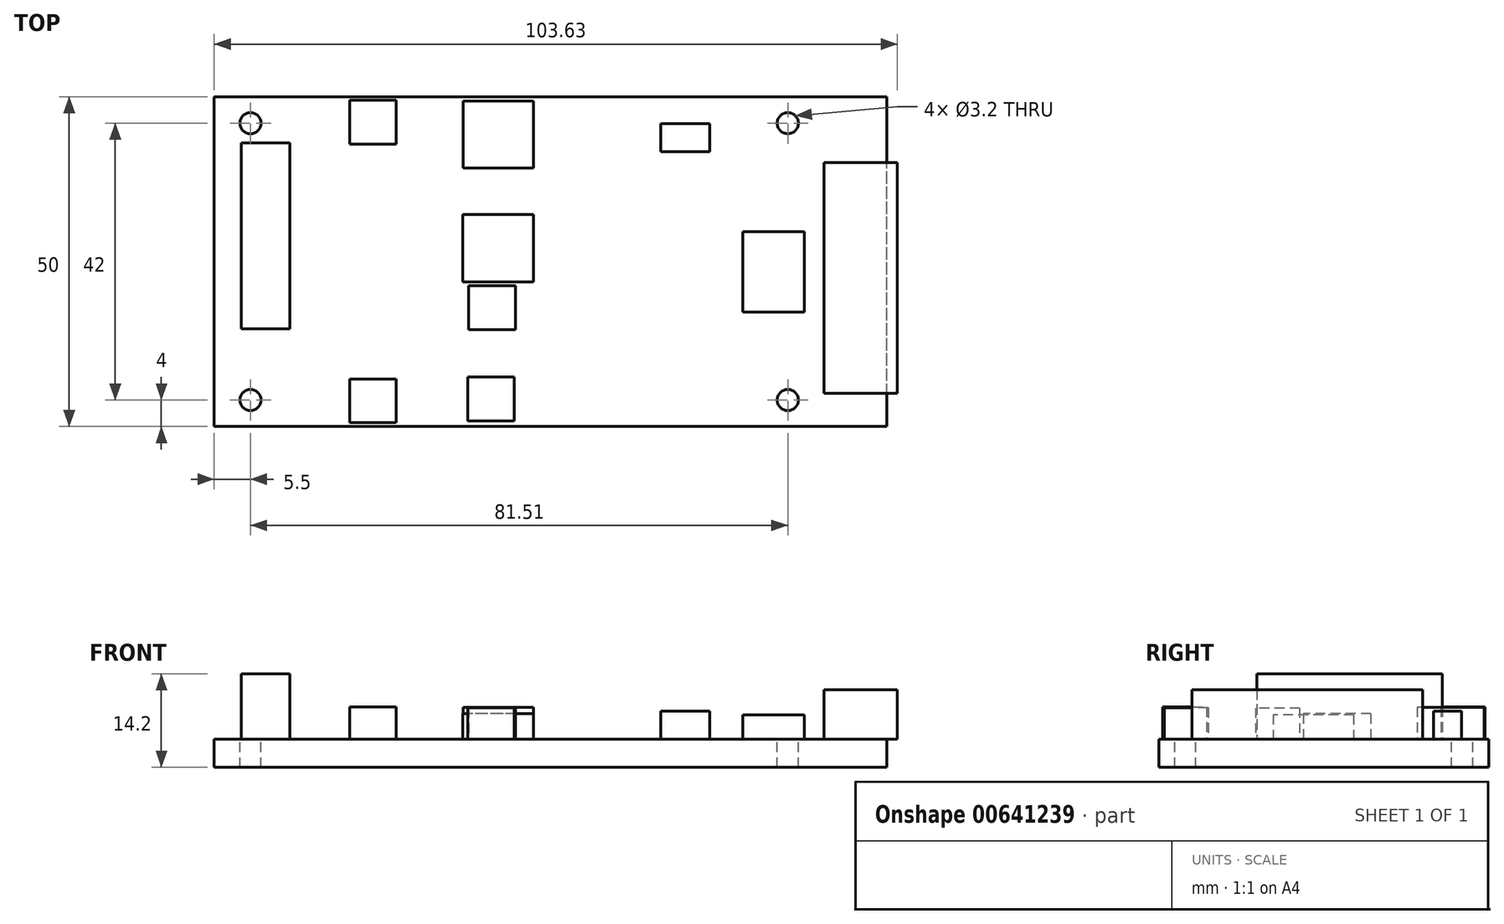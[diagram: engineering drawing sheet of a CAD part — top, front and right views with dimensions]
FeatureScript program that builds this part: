
annotation { "Feature Type Name" : "Feature", "Feature Type Description" : "" }
export const myFeature = defineFeature(function(context is Context, id is Id, definition is map)
    precondition{}
    {
        {
            var Q0;
            Q0=qCreatedBy(makeId("Top.planeOp"),FACE);
            var sketch = newSketch(context, id + "F0", { "sketchPlane" : qUnion([Q0])});
            skLineSegment(sketch, "E0.bottom", {"start": v(51, -25) * mm, "end": v(-51, -25) * mm});
            skLineSegment(sketch, "E0.top", {"start": v(51, 25) * mm, "end": v(-51, 25) * mm});
            skLineSegment(sketch, "E0.left", {"start": v(51, -25) * mm, "end": v(51, 25) * mm});
            skLineSegment(sketch, "E0.right", {"start": v(-51, -25) * mm, "end": v(-51, 25) * mm});
            skPoint(sketch, "E0.middle", {"position": v(0, 0) * mm});
            skSolve(sketch);
        }
        {
            var Q0;
            Q0 = qSketchRegion(id + "F0", true);
            extrude(context, id + "F1", {"entities" : qUnion([Q0]), "depth" : 4.27 * mm, "offsetDistance" : 25 * mm});
        }
        {
            var Q0;
            Q0=makeQuery(id+"F1.opExtrude","CAP_FACE",FACE,{"disambiguationData":[OSD([sQuery(id+"F0.wireOp",EDGE,"E0.bottom"),sQuery(id+"F0.wireOp",EDGE,"E0.top"),sQuery(id+"F0.wireOp",EDGE,"E0.left"),sQuery(id+"F0.wireOp",EDGE,"E0.right")])],"isStart":false});
            var sketch = newSketch(context, id + "F2", { "sketchPlane" : qUnion([Q0])});
            skLineSegment(sketch, "E1.bottom", {"start": v(41.53, 15) * mm, "end": v(52.63, 15) * mm});
            skLineSegment(sketch, "E1.top", {"start": v(41.53, -20) * mm, "end": v(52.63, -20) * mm});
            skLineSegment(sketch, "E1.left", {"start": v(41.53, 15) * mm, "end": v(41.53, -20) * mm});
            skLineSegment(sketch, "E1.right", {"start": v(52.63, 15) * mm, "end": v(52.63, -20) * mm});
            skSolve(sketch);
        }
        {
            var Q0;
            Q0 = qSketchRegion(id + "F2", true);
            extrude(context, id + "F3", {"entities" : qUnion([Q0]), "operationType" : NewBodyOperationType.ADD, "depth" : 7.5 * mm, "offsetDistance" : 25 * mm});
        }
        {
            var Q0;
            Q0=makeQuery(id+"F1.opExtrude","CAP_FACE",FACE,{"disambiguationData":[OSD([sQuery(id+"F0.wireOp",EDGE,"E0.bottom"),sQuery(id+"F0.wireOp",EDGE,"E0.top"),sQuery(id+"F0.wireOp",EDGE,"E0.left"),sQuery(id+"F0.wireOp",EDGE,"E0.right")])],"isStart":false});
            var sketch = newSketch(context, id + "F4", { "sketchPlane" : qUnion([Q0])});
            skLineSegment(sketch, "E2.bottom", {"start": v(-46.91, 17.98) * mm, "end": v(-39.54, 17.98) * mm});
            skLineSegment(sketch, "E2.top", {"start": v(-46.91, -10.17) * mm, "end": v(-39.54, -10.17) * mm});
            skLineSegment(sketch, "E2.left", {"start": v(-46.91, 17.98) * mm, "end": v(-46.91, -10.17) * mm});
            skLineSegment(sketch, "E2.right", {"start": v(-39.54, 17.98) * mm, "end": v(-39.54, -10.17) * mm});
            skSolve(sketch);
        }
        {
            var Q0;
            Q0 = qSketchRegion(id + "F4", true);
            extrude(context, id + "F5", {"entities" : qUnion([Q0]), "operationType" : NewBodyOperationType.ADD, "depth" : 9.93 * mm, "offsetDistance" : 25 * mm});
        }
        {
            var Q0;
            Q0=makeQuery(id+"F1.opExtrude","CAP_FACE",FACE,{"disambiguationData":[OSD([sQuery(id+"F0.wireOp",EDGE,"E0.bottom"),sQuery(id+"F0.wireOp",EDGE,"E0.top"),sQuery(id+"F0.wireOp",EDGE,"E0.left"),sQuery(id+"F0.wireOp",EDGE,"E0.right")])],"isStart":false});
            var sketch = newSketch(context, id + "F6", { "sketchPlane" : qUnion([Q0])});
            skLineSegment(sketch, "E3.bottom", {"start": v(-30.45, 24.45) * mm, "end": v(-23.37, 24.45) * mm});
            skLineSegment(sketch, "E3.top", {"start": v(-30.45, 17.79) * mm, "end": v(-23.37, 17.79) * mm});
            skLineSegment(sketch, "E3.left", {"start": v(-30.45, 24.45) * mm, "end": v(-30.45, 17.79) * mm});
            skLineSegment(sketch, "E3.right", {"start": v(-23.37, 24.45) * mm, "end": v(-23.37, 17.79) * mm});
            skSolve(sketch);
        }
        {
            var Q0;
            Q0 = qSketchRegion(id + "F6", true);
            extrude(context, id + "F7", {"entities" : qUnion([Q0]), "depth" : 4.88 * mm, "offsetDistance" : 25 * mm});
        }
        {
            var Q0;
            Q0=makeQuery(id+"F1.opExtrude","CAP_FACE",FACE,{"disambiguationData":[OSD([sQuery(id+"F0.wireOp",EDGE,"E0.bottom"),sQuery(id+"F0.wireOp",EDGE,"E0.top"),sQuery(id+"F0.wireOp",EDGE,"E0.left"),sQuery(id+"F0.wireOp",EDGE,"E0.right")])],"isStart":false});
            var sketch = newSketch(context, id + "F8", { "sketchPlane" : qUnion([Q0])});
            skLineSegment(sketch, "E4.bottom", {"start": v(-13.22, 24.32) * mm, "end": v(-2.57, 24.32) * mm});
            skLineSegment(sketch, "E4.top", {"start": v(-13.22, 14.17) * mm, "end": v(-2.57, 14.17) * mm});
            skLineSegment(sketch, "E4.left", {"start": v(-13.22, 24.32) * mm, "end": v(-13.22, 14.17) * mm});
            skLineSegment(sketch, "E4.right", {"start": v(-2.57, 24.32) * mm, "end": v(-2.57, 14.17) * mm});
            skSolve(sketch);
        }
        {
            var Q0;
            Q0 = qSketchRegion(id + "F8", true);
            extrude(context, id + "F9", {"entities" : qUnion([Q0]), "operationType" : NewBodyOperationType.ADD, "depth" : 4.85 * mm, "offsetDistance" : 25 * mm});
        }
        {
            var Q0;
            Q0=makeQuery(id+"F1.opExtrude","CAP_FACE",FACE,{"disambiguationData":[OSD([sQuery(id+"F0.wireOp",EDGE,"E0.bottom"),sQuery(id+"F0.wireOp",EDGE,"E0.top"),sQuery(id+"F0.wireOp",EDGE,"E0.left"),sQuery(id+"F0.wireOp",EDGE,"E0.right")])],"isStart":false});
            var sketch = newSketch(context, id + "F10", { "sketchPlane" : qUnion([Q0])});
            skLineSegment(sketch, "E5.bottom", {"start": v(-2.57, 7.13) * mm, "end": v(-13.28, 7.13) * mm});
            skLineSegment(sketch, "E5.top", {"start": v(-2.57, -3.1) * mm, "end": v(-13.28, -3.1) * mm});
            skLineSegment(sketch, "E5.left", {"start": v(-2.57, 7.13) * mm, "end": v(-2.57, -3.09) * mm});
            skLineSegment(sketch, "E5.right", {"start": v(-13.28, 7.13) * mm, "end": v(-13.28, -3.1) * mm});
            skSolve(sketch);
        }
        {
            var Q0;
            Q0 = qSketchRegion(id + "F10", true);
            extrude(context, id + "F11", {"entities" : qUnion([Q0]), "operationType" : NewBodyOperationType.ADD, "depth" : 3.86 * mm, "offsetDistance" : 25 * mm});
        }
        {
            var Q0;
            Q0=makeQuery(id+"F7.opExtrude","SWEPT_BODY",BODY,{"disambiguationData":[OSD([sQuery(id+"F6.wireOp",EDGE,"E3.bottom"),sQuery(id+"F6.wireOp",EDGE,"E3.top"),sQuery(id+"F6.wireOp",EDGE,"E3.left"),sQuery(id+"F6.wireOp",EDGE,"E3.right")])]});
            var Q1;
            Q1=qCreatedBy(makeId("Front.planeOp"),FACE);
            mirror(context, id + "F12", {"entities" : qUnion([Q0]), "mirrorPlane" : qUnion([Q1])});
        }
        {
            var Q0;
            Q0=makeQuery(id+"F1.opExtrude","CAP_FACE",FACE,{"disambiguationData":[OSD([sQuery(id+"F0.wireOp",EDGE,"E0.bottom"),sQuery(id+"F0.wireOp",EDGE,"E0.top"),sQuery(id+"F0.wireOp",EDGE,"E0.left"),sQuery(id+"F0.wireOp",EDGE,"E0.right")])],"isStart":false});
            var sketch = newSketch(context, id + "F13", { "sketchPlane" : qUnion([Q0])});
            skLineSegment(sketch, "E6.bottom", {"start": v(-12.4, -3.65) * mm, "end": v(-5.32, -3.65) * mm});
            skLineSegment(sketch, "E6.top", {"start": v(-12.4, -10.31) * mm, "end": v(-5.32, -10.31) * mm});
            skLineSegment(sketch, "E6.left", {"start": v(-12.4, -3.65) * mm, "end": v(-12.4, -10.31) * mm});
            skLineSegment(sketch, "E6.right", {"start": v(-5.32, -3.65) * mm, "end": v(-5.32, -10.31) * mm});
            skSolve(sketch);
        }
        {
            var Q0;
            Q0 = qSketchRegion(id + "F13", true);
            extrude(context, id + "F14", {"entities" : qUnion([Q0]), "operationType" : NewBodyOperationType.ADD, "depth" : 4.73 * mm, "offsetDistance" : 25 * mm});
        }
        {
            var Q0;
            Q0=makeQuery(id+"F1.opExtrude","CAP_FACE",FACE,{"disambiguationData":[OSD([sQuery(id+"F0.wireOp",EDGE,"E0.bottom"),sQuery(id+"F0.wireOp",EDGE,"E0.top"),sQuery(id+"F0.wireOp",EDGE,"E0.left"),sQuery(id+"F0.wireOp",EDGE,"E0.right")])],"isStart":false});
            var sketch = newSketch(context, id + "F15", { "sketchPlane" : qUnion([Q0])});
            skLineSegment(sketch, "E7.bottom", {"start": v(-12.54, -17.5) * mm, "end": v(-5.46, -17.5) * mm});
            skLineSegment(sketch, "E7.top", {"start": v(-12.54, -24.17) * mm, "end": v(-5.46, -24.17) * mm});
            skLineSegment(sketch, "E7.left", {"start": v(-12.54, -17.5) * mm, "end": v(-12.54, -24.17) * mm});
            skLineSegment(sketch, "E7.right", {"start": v(-5.46, -17.5) * mm, "end": v(-5.46, -24.17) * mm});
            skSolve(sketch);
        }
        {
            var Q0;
            Q0 = qSketchRegion(id + "F15", true);
            extrude(context, id + "F16", {"entities" : qUnion([Q0]), "operationType" : NewBodyOperationType.ADD, "depth" : 4.75 * mm, "offsetDistance" : 25 * mm});
        }
        {
            var Q0;
            Q0=makeQuery(id+"F1.opExtrude","CAP_FACE",FACE,{"disambiguationData":[OSD([sQuery(id+"F0.wireOp",EDGE,"E0.bottom"),sQuery(id+"F0.wireOp",EDGE,"E0.top"),sQuery(id+"F0.wireOp",EDGE,"E0.left"),sQuery(id+"F0.wireOp",EDGE,"E0.right")])],"isStart":false});
            var sketch = newSketch(context, id + "F17", { "sketchPlane" : qUnion([Q0])});
            skLineSegment(sketch, "E8.bottom", {"start": v(29.2, 4.54) * mm, "end": v(38.5, 4.54) * mm});
            skLineSegment(sketch, "E8.top", {"start": v(29.2, -7.65) * mm, "end": v(38.5, -7.65) * mm});
            skLineSegment(sketch, "E8.left", {"start": v(29.2, 4.54) * mm, "end": v(29.2, -7.65) * mm});
            skLineSegment(sketch, "E8.right", {"start": v(38.5, 4.54) * mm, "end": v(38.5, -7.65) * mm});
            skSolve(sketch);
        }
        {
            var Q0;
            Q0 = qSketchRegion(id + "F17", true);
            extrude(context, id + "F18", {"entities" : qUnion([Q0]), "operationType" : NewBodyOperationType.ADD, "depth" : 3.7 * mm, "offsetDistance" : 25 * mm});
        }
        {
            var Q0;
            Q0=makeQuery(id+"F1.opExtrude","CAP_FACE",FACE,{"disambiguationData":[OSD([sQuery(id+"F0.wireOp",EDGE,"E0.bottom"),sQuery(id+"F0.wireOp",EDGE,"E0.top"),sQuery(id+"F0.wireOp",EDGE,"E0.left"),sQuery(id+"F0.wireOp",EDGE,"E0.right")])],"isStart":false});
            var sketch = newSketch(context, id + "F19", { "sketchPlane" : qUnion([Q0])});
            skLineSegment(sketch, "E9.bottom", {"start": v(16.75, 20.9) * mm, "end": v(24.17, 20.9) * mm});
            skLineSegment(sketch, "E9.top", {"start": v(16.75, 16.67) * mm, "end": v(24.17, 16.67) * mm});
            skLineSegment(sketch, "E9.left", {"start": v(16.75, 20.9) * mm, "end": v(16.75, 16.67) * mm});
            skLineSegment(sketch, "E9.right", {"start": v(24.17, 20.9) * mm, "end": v(24.17, 16.67) * mm});
            skSolve(sketch);
        }
        {
            var Q0;
            Q0 = qSketchRegion(id + "F19", true);
            extrude(context, id + "F20", {"entities" : qUnion([Q0]), "operationType" : NewBodyOperationType.ADD, "depth" : 4.23 * mm, "offsetDistance" : 25 * mm});
        }
        {
            var Q0;
            Q0=makeQuery(id+"F1.opExtrude","CAP_FACE",FACE,{"disambiguationData":[OSD([sQuery(id+"F0.wireOp",EDGE,"E0.bottom"),sQuery(id+"F0.wireOp",EDGE,"E0.top"),sQuery(id+"F0.wireOp",EDGE,"E0.left"),sQuery(id+"F0.wireOp",EDGE,"E0.right")])],"isStart":false});
            var sketch = newSketch(context, id + "F21", { "sketchPlane" : qUnion([Q0])});
            skCircle(sketch, "E10", {"center": v(-45.5, -21) * mm, "radius": 1.6 * mm});
            skCircle(sketch, "E11", {"center": v(36.01, -21) * mm, "radius": 1.6 * mm});
            skCircle(sketch, "E12.MirrorC", {"center": v(-45.5, 21) * mm, "radius": 1.6 * mm});
            skCircle(sketch, "E13.MirrorC", {"center": v(36.01, 21) * mm, "radius": 1.6 * mm});
            skSolve(sketch);
        }
        {
            var Q0;
            Q0 = qSketchRegion(id + "F21", true);
            extrude(context, id + "F22", {"entities" : qUnion([Q0]), "operationType" : NewBodyOperationType.REMOVE, "oppositeDirection" : true, "depth" : 25 * mm, "offsetDistance" : 25 * mm});
        }
    });
